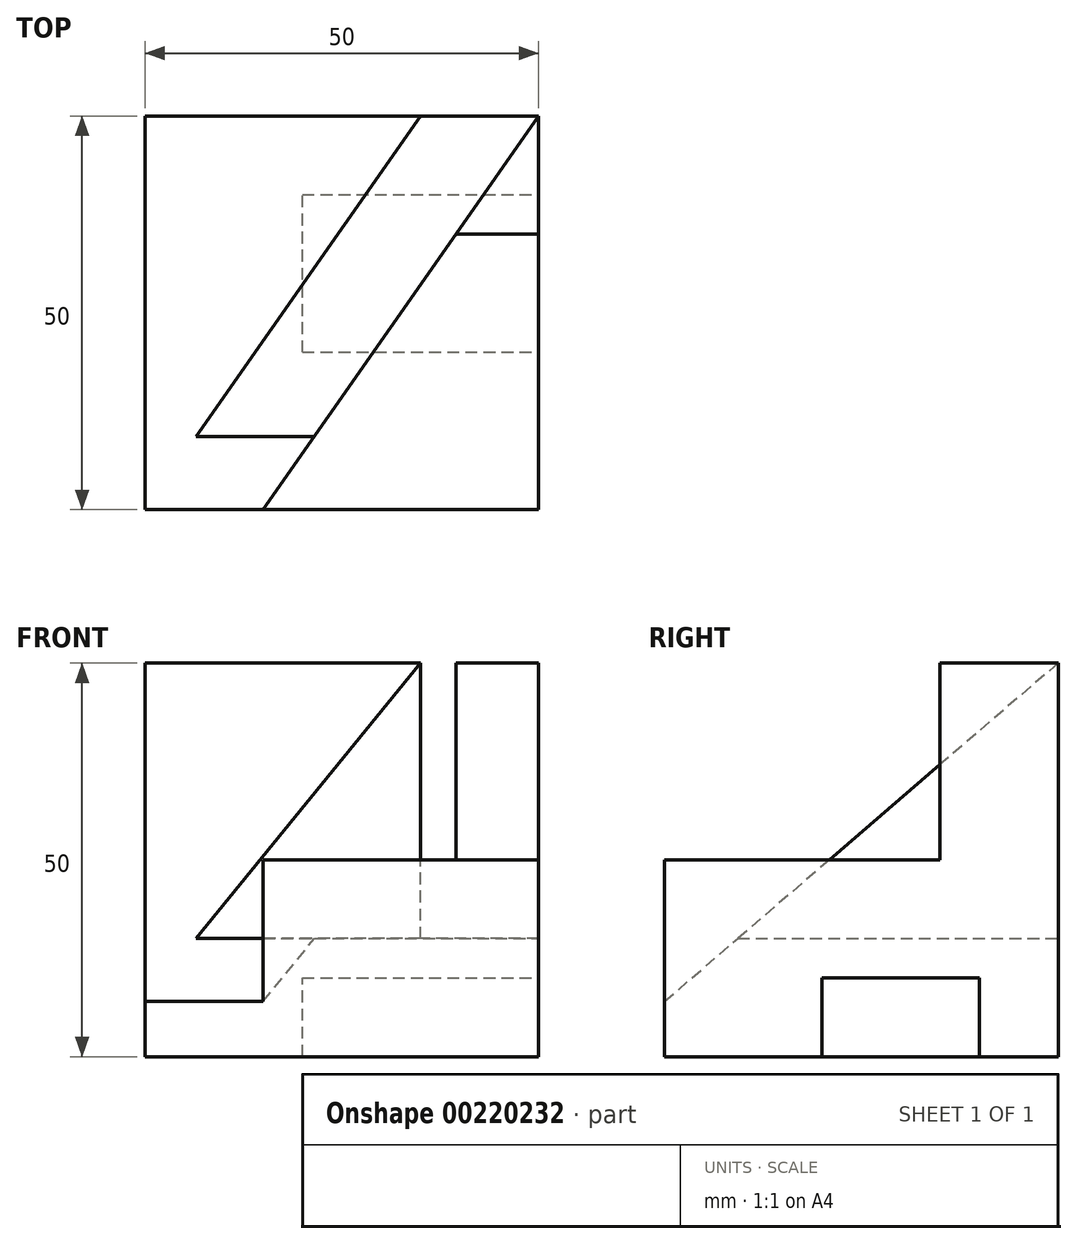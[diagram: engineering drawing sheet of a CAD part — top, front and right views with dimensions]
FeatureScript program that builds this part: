
annotation { "Feature Type Name" : "Feature", "Feature Type Description" : "" }
export const myFeature = defineFeature(function(context is Context, id is Id, definition is map)
    precondition{}
    {
        {
            var Q0;
            Q0=qCreatedBy(makeId("Right.planeOp"),FACE);
            var sketch = newSketch(context, id + "F0", { "sketchPlane" : qUnion([Q0])});
            skLineSegment(sketch, "E0", {"start": v(0, 0) * mm, "end": v(0, 50) * mm});
            skLineSegment(sketch, "E1", {"start": v(0, 50) * mm, "end": v(-15, 50) * mm});
            skLineSegment(sketch, "E2", {"start": v(-15, 50) * mm, "end": v(-15, 25) * mm});
            skLineSegment(sketch, "E3", {"start": v(-15, 25) * mm, "end": v(-50, 25) * mm});
            skLineSegment(sketch, "E4", {"start": v(-50, 25) * mm, "end": v(-50, 0) * mm});
            skLineSegment(sketch, "E5", {"start": v(-50, 0) * mm, "end": v(0, 0) * mm});
            skSolve(sketch);
        }
        {
            var Q0;
            Q0 = qSketchRegion(id + "F0", true);
            extrude(context, id + "F1", {"entities" : qUnion([Q0]), "oppositeDirection" : true, "depth" : 50 * mm});
        }
        {
            var Q0;
            Q0=makeQuery(id+"F1.opExtrude","SWEPT_FACE",FACE,{"disambiguationData":[OSD([sQuery(id+"F0.wireOp",EDGE,"E1")])]});
            var sketch = newSketch(context, id + "F2", { "sketchPlane" : qUnion([Q0])});
            skLineSegment(sketch, "E6", {"start": v(-50, 0) * mm, "end": v(0, 0) * mm});
            skLineSegment(sketch, "E7", {"start": v(0, 0) * mm, "end": v(-35, -50) * mm});
            skLineSegment(sketch, "E8", {"start": v(-35, -50) * mm, "end": v(-50, -50) * mm});
            skLineSegment(sketch, "E9", {"start": v(-50, -50) * mm, "end": v(-50, 0) * mm});
            skSolve(sketch);
        }
        {
            var Q0;
            Q0=makeQuery(id+"F1.opExtrude","SWEPT_FACE",FACE,{"disambiguationData":[OSD([sQuery(id+"F0.wireOp",EDGE,"E5")])]});
            cPlane(context, id + "F3", {"entities" : qUnion([Q0]), "cplaneType" : CPlaneType.OFFSET, "offset" : 7 * mm, "oppositeDirection" : true, "width" : 150 * mm, "height" : 150 * mm});
        }
        {
            var Q0;
            Q0 = qSketchRegion(id + "F2", true);
            var Q1;
            Q1=qCreatedBy(id+"F3.planeOp",FACE);
            extrude(context, id + "F4", {"entities" : qUnion([Q0]), "operationType" : NewBodyOperationType.REMOVE, "endBound" : BoundingType.UP_TO_SURFACE, "oppositeDirection" : true, "endBoundEntityFace" : qUnion([Q1]), "depth" : 25 * mm});
        }
        {
            var Q0;
            Q0=qCreatedBy(makeId("Right.planeOp"),FACE);
            var Q1;
            Q1=makeQuery(id+"F1.opExtrude","CAP_VERTEX",VERTEX,{"disambiguationData":[OSD([sQuery(id+"F0.wireOp",EDGE,"E4"),sQuery(id+"F0.wireOp",EDGE,"E5")])],"isStart":false});
            cPlane(context, id + "F5", {"entities" : qUnion([Q0, Q1]), "cplaneType" : CPlaneType.PLANE_POINT, "offset" : 25 * mm, "width" : 150 * mm, "height" : 150 * mm});
        }
        {
            var Q0;
            Q0=qCreatedBy(id+"F5.planeOp",FACE);
            var sketch = newSketch(context, id + "F6", { "sketchPlane" : qUnion([Q0])});
            skLineSegment(sketch, "E10", {"start": v(0, 7) * mm, "end": v(0, 50) * mm});
            skLineSegment(sketch, "E11", {"start": v(0, 50) * mm, "end": v(-50, 7) * mm});
            skLineSegment(sketch, "E12", {"start": v(-50, 7) * mm, "end": v(0, 7) * mm});
            skSolve(sketch);
        }
        {
            var Q0;
            Q0=makeQuery(id+"F6.imprint","IMPRINT",FACE,{"disambiguationData":[TD([[makeQuery(id+"F6.imprint","IMPRINT",EDGE,{"derivedFrom":sQuery(id+"F6.wireOp",EDGE,"E10")}),1.0]])]});
            var Q1;
            Q1=makeQuery(id+"F4.boolean.opBoolean","COPY",FACE,{"derivedFrom":makeQuery(id+"F4.opExtrude","SWEPT_FACE",FACE,{"disambiguationData":[OSD([sQuery(id+"F2.wireOp",EDGE,"E7")])]})});
            extrude(context, id + "F7", {"entities" : qUnion([Q0]), "operationType" : NewBodyOperationType.ADD, "endBound" : BoundingType.UP_TO_SURFACE, "endBoundEntityFace" : qUnion([Q1]), "depth" : 25 * mm});
        }
        {
            var Q0;
            Q0=qCreatedBy(makeId("Top.planeOp"),FACE);
            var Q1;
            Q1=makeQuery(id+"F7.opExtrude","CAP_VERTEX",VERTEX,{"disambiguationData":[OSD([sQuery(id+"F6.wireOp",EDGE,"E10"),sQuery(id+"F6.wireOp",EDGE,"E11")])],"isStart":true});
            cPlane(context, id + "F8", {"entities" : qUnion([Q0, Q1]), "cplaneType" : CPlaneType.PLANE_POINT, "offset" : 25 * mm, "width" : 150 * mm, "height" : 150 * mm});
        }
        {
            var Q0;
            Q0=qCreatedBy(id+"F8.planeOp",FACE);
            var sketch = newSketch(context, id + "F9", { "sketchPlane" : qUnion([Q0])});
            skLineSegment(sketch, "E13", {"start": v(-15, 0) * mm, "end": v(0, 0) * mm});
            skLineSegment(sketch, "E14", {"start": v(0, 0) * mm, "end": v(-35, -50) * mm});
            skLineSegment(sketch, "E15", {"start": v(-35, -50) * mm, "end": v(-50, -50) * mm});
            skLineSegment(sketch, "E16", {"start": v(-50, -50) * mm, "end": v(-15, 0) * mm});
            skSolve(sketch);
        }
        {
            var Q0;
            Q0=qCreatedBy(makeId("Top.planeOp"),FACE);
            cPlane(context, id + "F10", {"entities" : qUnion([Q0]), "cplaneType" : CPlaneType.OFFSET, "offset" : 15 * mm, "width" : 150 * mm, "height" : 150 * mm});
        }
        {
            var Q0;
            Q0 = qSketchRegion(id + "F9", true);
            var Q1;
            Q1=qCreatedBy(id+"F10.planeOp",FACE);
            extrude(context, id + "F11", {"entities" : qUnion([Q0]), "operationType" : NewBodyOperationType.REMOVE, "endBound" : BoundingType.UP_TO_SURFACE, "oppositeDirection" : true, "endBoundEntityFace" : qUnion([Q1]), "depth" : 25 * mm});
        }
        {
            var Q0;
            Q0=makeQuery(id+"F1.opExtrude","CAP_FACE",FACE,{"disambiguationData":[OSD([sQuery(id+"F0.wireOp",EDGE,"E0"),sQuery(id+"F0.wireOp",EDGE,"E1"),sQuery(id+"F0.wireOp",EDGE,"E2"),sQuery(id+"F0.wireOp",EDGE,"E3"),sQuery(id+"F0.wireOp",EDGE,"E4"),sQuery(id+"F0.wireOp",EDGE,"E5")])],"isStart":true});
            var sketch = newSketch(context, id + "F12", { "sketchPlane" : qUnion([Q0])});
            skLineSegment(sketch, "E17.bottom", {"start": v(-30, 0) * mm, "end": v(-10, 0) * mm});
            skLineSegment(sketch, "E17.top", {"start": v(-30, 10) * mm, "end": v(-10, 10) * mm});
            skLineSegment(sketch, "E17.left", {"start": v(-30, 0) * mm, "end": v(-30, 10) * mm});
            skLineSegment(sketch, "E17.right", {"start": v(-10, 0) * mm, "end": v(-10, 10) * mm});
            skSolve(sketch);
        }
        {
            var Q0;
            Q0=makeQuery(id+"F1.opExtrude","CAP_FACE",FACE,{"disambiguationData":[OSD([sQuery(id+"F0.wireOp",EDGE,"E0"),sQuery(id+"F0.wireOp",EDGE,"E1"),sQuery(id+"F0.wireOp",EDGE,"E2"),sQuery(id+"F0.wireOp",EDGE,"E3"),sQuery(id+"F0.wireOp",EDGE,"E4"),sQuery(id+"F0.wireOp",EDGE,"E5")])],"isStart":false});
            cPlane(context, id + "F13", {"entities" : qUnion([Q0]), "cplaneType" : CPlaneType.OFFSET, "offset" : 20 * mm, "oppositeDirection" : true, "width" : 150 * mm, "height" : 150 * mm});
        }
        {
            var Q0;
            Q0=makeQuery(id+"F12.imprint","IMPRINT",FACE,{"disambiguationData":[TD([[makeQuery(id+"F12.imprint","IMPRINT",EDGE,{"derivedFrom":sQuery(id+"F12.wireOp",EDGE,"E17.bottom")}),1.0]])]});
            var Q1;
            Q1=qCreatedBy(id+"F13.planeOp",FACE);
            extrude(context, id + "F14", {"entities" : qUnion([Q0]), "operationType" : NewBodyOperationType.REMOVE, "endBound" : BoundingType.UP_TO_SURFACE, "oppositeDirection" : true, "endBoundEntityFace" : qUnion([Q1]), "depth" : 25 * mm});
        }
    });
